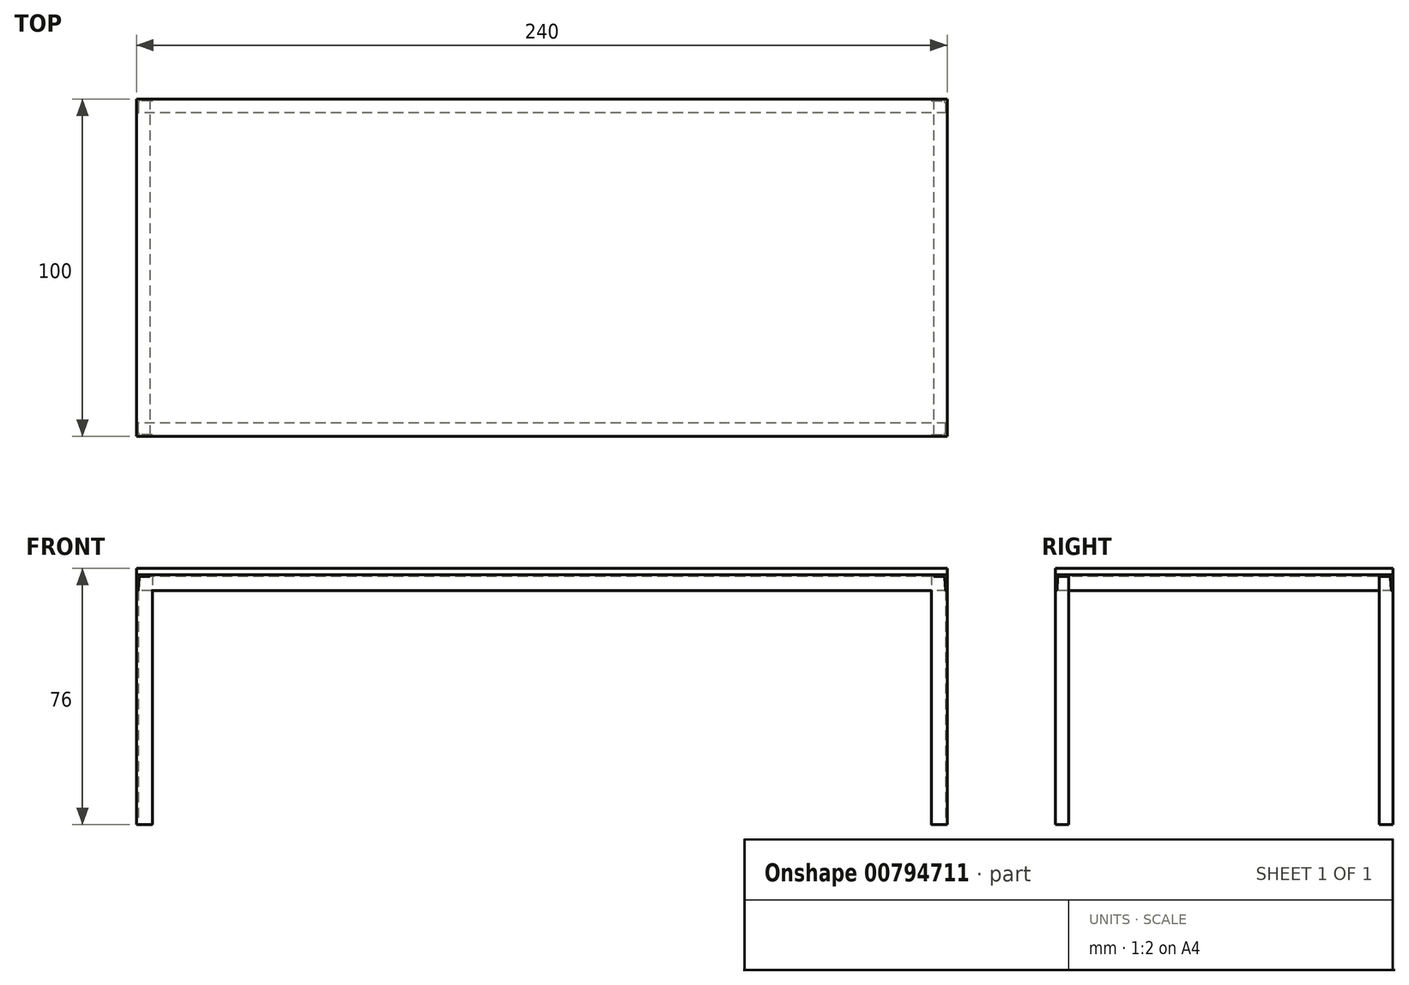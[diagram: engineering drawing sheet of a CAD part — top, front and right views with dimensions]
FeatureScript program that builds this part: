
annotation { "Feature Type Name" : "Feature", "Feature Type Description" : "" }
export const myFeature = defineFeature(function(context is Context, id is Id, definition is map)
    precondition{}
    {
        {
            var Q0;
            Q0=qCreatedBy(makeId("Top.planeOp"),FACE);
            var sketch = newSketch(context, id + "F0", { "sketchPlane" : qUnion([Q0])});
            skLineSegment(sketch, "E0", {"start": v(0, 0) * mm, "end": v(0, 4) * mm});
            skLineSegment(sketch, "E1", {"start": v(0, 4) * mm, "end": v(0, 0) * mm});
            skLineSegment(sketch, "E2", {"start": v(0, 0) * mm, "end": v(4.52, 0) * mm});
            skLineSegment(sketch, "E3", {"start": v(0.5, 1.22) * mm, "end": v(0.5, 4) * mm});
            skLineSegment(sketch, "E4", {"start": v(4.53, 0.51) * mm, "end": v(0.97, 0.72) * mm});
            skLineSegment(sketch, "E5", {"start": v(4.7, 0.33) * mm, "end": v(4.7, 0.18) * mm});
            skLineSegment(sketch, "E6", {"start": v(0, 4) * mm, "end": v(0.5, 4) * mm});
            skPoint(sketch, "E7.visualSharp", {"position": v(0.5, 0.75) * mm});
            skArc(sketch, "E7.filletArc", {"start": v(0.5, 1.22) * mm, "mid": v(0.64, 0.88) * mm, "end": v(0.97, 0.72) * mm});
            skPoint(sketch, "E8.visualSharp", {"position": v(4.7, 0.5) * mm});
            skArc(sketch, "E8.filletArc", {"start": v(4.7, 0.33) * mm, "mid": v(4.65, 0.45) * mm, "end": v(4.53, 0.51) * mm});
            skPoint(sketch, "E9.visualSharp", {"position": v(4.7, 0) * mm});
            skArc(sketch, "E9.filletArc", {"start": v(4.52, 0) * mm, "mid": v(4.65, 0.05) * mm, "end": v(4.7, 0.18) * mm});
            skSolve(sketch);
        }
        {
            var Q0;
            Q0 = qSketchRegion(id + "F0", true);
            extrude(context, id + "F1", {"entities" : qUnion([Q0]), "depth" : 74 * mm, "offsetDistance" : 25 * mm});
        }
        {
            var Q0;
            Q0=qCreatedBy(makeId("Front.planeOp"),FACE);
            cPlane(context, id + "F2", {"entities" : qUnion([Q0]), "cplaneType" : CPlaneType.OFFSET, "offset" : 50 * mm, "oppositeDirection" : true, "width" : 150 * mm, "height" : 150 * mm});
        }
        {
            var Q0;
            Q0=makeQuery(id+"F1.opExtrude","SWEPT_BODY",BODY,{"disambiguationData":[OSD([sQuery(id+"F0.wireOp",EDGE,"E1"),sQuery(id+"F0.wireOp",EDGE,"E2"),sQuery(id+"F0.wireOp",EDGE,"E3"),sQuery(id+"F0.wireOp",EDGE,"E4"),sQuery(id+"F0.wireOp",EDGE,"E5"),sQuery(id+"F0.wireOp",EDGE,"E6"),sQuery(id+"F0.wireOp",EDGE,"E7.filletArc"),sQuery(id+"F0.wireOp",EDGE,"E8.filletArc"),sQuery(id+"F0.wireOp",EDGE,"E9.filletArc")])]});
            var Q1;
            Q1=qCreatedBy(id+"F2.planeOp",FACE);
            mirror(context, id + "F3", {"entities" : qUnion([Q0]), "mirrorPlane" : qUnion([Q1])});
        }
        {
            var Q0;
            Q0=qCreatedBy(makeId("Right.planeOp"),FACE);
            cPlane(context, id + "F4", {"entities" : qUnion([Q0]), "cplaneType" : CPlaneType.OFFSET, "offset" : 120 * mm, "width" : 150 * mm, "height" : 150 * mm});
        }
        {
            var Q0;
            Q0=makeQuery(id+"F1.opExtrude","SWEPT_BODY",BODY,{"disambiguationData":[OSD([sQuery(id+"F0.wireOp",EDGE,"E1"),sQuery(id+"F0.wireOp",EDGE,"E2"),sQuery(id+"F0.wireOp",EDGE,"E3"),sQuery(id+"F0.wireOp",EDGE,"E4"),sQuery(id+"F0.wireOp",EDGE,"E5"),sQuery(id+"F0.wireOp",EDGE,"E6"),sQuery(id+"F0.wireOp",EDGE,"E7.filletArc"),sQuery(id+"F0.wireOp",EDGE,"E8.filletArc"),sQuery(id+"F0.wireOp",EDGE,"E9.filletArc")])]});
            var Q1;
            Q1=makeQuery(id+"F3.opPattern","COPY",BODY,{"derivedFrom":makeQuery(id+"F1.opExtrude","SWEPT_BODY",BODY,{"disambiguationData":[OSD([sQuery(id+"F0.wireOp",EDGE,"E1"),sQuery(id+"F0.wireOp",EDGE,"E2"),sQuery(id+"F0.wireOp",EDGE,"E3"),sQuery(id+"F0.wireOp",EDGE,"E4"),sQuery(id+"F0.wireOp",EDGE,"E5"),sQuery(id+"F0.wireOp",EDGE,"E6"),sQuery(id+"F0.wireOp",EDGE,"E7.filletArc"),sQuery(id+"F0.wireOp",EDGE,"E8.filletArc"),sQuery(id+"F0.wireOp",EDGE,"E9.filletArc")])]}),"instanceName":"1"});
            var Q2;
            Q2=qCreatedBy(id+"F4.planeOp",FACE);
            mirror(context, id + "F5", {"entities" : qUnion([Q0, Q1]), "mirrorPlane" : qUnion([Q2])});
        }
        {
            var Q0;
            Q0=qCreatedBy(makeId("Right.planeOp"),FACE);
            var sketch = newSketch(context, id + "F6", { "sketchPlane" : qUnion([Q0])});
            skArc(sketch, "E10.1.0", {"start": v(0.33, 69.3) * mm, "mid": v(0.45, 69.35) * mm, "end": v(0.51, 69.47) * mm});
            skLineSegment(sketch, "E10.1.1", {"start": v(1.22, 73.5) * mm, "end": v(4, 73.5) * mm});
            skLineSegment(sketch, "E10.1.2", {"start": v(4, 74) * mm, "end": v(0, 74) * mm});
            skLineSegment(sketch, "E10.1.3", {"start": v(4, 74) * mm, "end": v(4, 73.5) * mm});
            skLineSegment(sketch, "E10.1.4", {"start": v(0.33, 69.3) * mm, "end": v(0.18, 69.3) * mm});
            skLineSegment(sketch, "E10.1.5", {"start": v(0.51, 69.47) * mm, "end": v(0.72, 73.03) * mm});
            skArc(sketch, "E10.1.6", {"start": v(1.22, 73.5) * mm, "mid": v(0.88, 73.36) * mm, "end": v(0.72, 73.03) * mm});
            skLineSegment(sketch, "E10.1.7", {"start": v(0, 74) * mm, "end": v(0, 69.48) * mm});
            skArc(sketch, "E10.1.8", {"start": v(0, 69.48) * mm, "mid": v(0.05, 69.35) * mm, "end": v(0.18, 69.3) * mm});
            skSolve(sketch);
        }
        {
            var Q0;
            Q0=makeQuery(id+"F6.imprint","IMPRINT",FACE,{"disambiguationData":[TD([[makeQuery(id+"F6.imprint","IMPRINT",EDGE,{"derivedFrom":sQuery(id+"F6.wireOp",EDGE,"E10.1.0")}),1.0]])]});
            extrude(context, id + "F7", {"entities" : qUnion([Q0]), "depth" : 240 * mm, "offsetDistance" : 25 * mm});
        }
        {
            var Q0;
            Q0=qCreatedBy(makeId("Front.planeOp"),FACE);
            cPlane(context, id + "F8", {"entities" : qUnion([Q0]), "cplaneType" : CPlaneType.OFFSET, "offset" : 50 * mm, "oppositeDirection" : true, "width" : 150 * mm, "height" : 150 * mm});
        }
        {
            var Q0;
            Q0=makeQuery(id+"F7.opExtrude","SWEPT_BODY",BODY,{"disambiguationData":[OSD([sQuery(id+"F6.wireOp",EDGE,"E10.1.0"),sQuery(id+"F6.wireOp",EDGE,"E10.1.1"),sQuery(id+"F6.wireOp",EDGE,"E10.1.2"),sQuery(id+"F6.wireOp",EDGE,"E10.1.3"),sQuery(id+"F6.wireOp",EDGE,"E10.1.4"),sQuery(id+"F6.wireOp",EDGE,"E10.1.5"),sQuery(id+"F6.wireOp",EDGE,"E10.1.6"),sQuery(id+"F6.wireOp",EDGE,"E10.1.7"),sQuery(id+"F6.wireOp",EDGE,"E10.1.8")])]});
            var Q1;
            Q1=qCreatedBy(id+"F8.planeOp",FACE);
            mirror(context, id + "F9", {"entities" : qUnion([Q0]), "mirrorPlane" : qUnion([Q1])});
        }
        {
            var Q0;
            Q0=qCreatedBy(makeId("Front.planeOp"),FACE);
            var sketch = newSketch(context, id + "F10", { "sketchPlane" : qUnion([Q0])});
            skArc(sketch, "E11.1.0", {"start": v(0.33, 69.3) * mm, "mid": v(0.45, 69.35) * mm, "end": v(0.51, 69.47) * mm});
            skLineSegment(sketch, "E11.1.1", {"start": v(1.22, 73.5) * mm, "end": v(4, 73.5) * mm});
            skLineSegment(sketch, "E11.1.3", {"start": v(4, 74) * mm, "end": v(4, 73.5) * mm});
            skLineSegment(sketch, "E11.1.4", {"start": v(0.33, 69.3) * mm, "end": v(0.18, 69.3) * mm});
            skLineSegment(sketch, "E11.1.5", {"start": v(0.51, 69.47) * mm, "end": v(0.72, 73.03) * mm});
            skArc(sketch, "E11.1.6", {"start": v(1.22, 73.5) * mm, "mid": v(0.88, 73.36) * mm, "end": v(0.72, 73.03) * mm});
            skLineSegment(sketch, "E11.1.7", {"start": v(0, 74) * mm, "end": v(0, 69.48) * mm});
            skArc(sketch, "E11.1.8", {"start": v(0, 69.48) * mm, "mid": v(0.05, 69.35) * mm, "end": v(0.18, 69.3) * mm});
            skLineSegment(sketch, "E12", {"start": v(0, 74) * mm, "end": v(4, 74) * mm});
            skSolve(sketch);
        }
        {
            var Q0;
            Q0=makeQuery(id+"F10.imprint","IMPRINT",FACE,{"disambiguationData":[TD([[makeQuery(id+"F10.imprint","IMPRINT",EDGE,{"derivedFrom":sQuery(id+"F10.wireOp",EDGE,"E11.1.0")}),1.0]])]});
            extrude(context, id + "F11", {"entities" : qUnion([Q0]), "oppositeDirection" : true, "depth" : 100 * mm, "offsetDistance" : 25 * mm});
        }
        {
            var Q0;
            Q0=qCreatedBy(makeId("Right.planeOp"),FACE);
            cPlane(context, id + "F12", {"entities" : qUnion([Q0]), "cplaneType" : CPlaneType.OFFSET, "offset" : 120 * mm, "width" : 150 * mm, "height" : 150 * mm});
        }
        {
            var Q0;
            Q0=makeQuery(id+"F11.opExtrude","SWEPT_BODY",BODY,{"disambiguationData":[OSD([sQuery(id+"F10.wireOp",EDGE,"E11.1.0"),sQuery(id+"F10.wireOp",EDGE,"E11.1.1"),sQuery(id+"F10.wireOp",EDGE,"E11.1.3"),sQuery(id+"F10.wireOp",EDGE,"E11.1.4"),sQuery(id+"F10.wireOp",EDGE,"E11.1.5"),sQuery(id+"F10.wireOp",EDGE,"E11.1.6"),sQuery(id+"F10.wireOp",EDGE,"E11.1.7"),sQuery(id+"F10.wireOp",EDGE,"E11.1.8"),sQuery(id+"F10.wireOp",EDGE,"E12")])]});
            var Q1;
            Q1=qCreatedBy(id+"F12.planeOp",FACE);
            mirror(context, id + "F13", {"entities" : qUnion([Q0]), "mirrorPlane" : qUnion([Q1])});
        }
        {
            var Q0;
            Q0=qCreatedBy(makeId("Top.planeOp"),FACE);
            var sketch = newSketch(context, id + "F14", { "sketchPlane" : qUnion([Q0])});
            skLineSegment(sketch, "E13.bottom", {"start": v(0, 100) * mm, "end": v(240, 100) * mm});
            skLineSegment(sketch, "E13.top", {"start": v(0, 0) * mm, "end": v(240, 0) * mm});
            skLineSegment(sketch, "E13.left", {"start": v(0, 100) * mm, "end": v(0, 0) * mm});
            skLineSegment(sketch, "E13.right", {"start": v(240, 100) * mm, "end": v(240, 0) * mm});
            skSolve(sketch);
        }
        {
            var Q0;
            Q0=makeQuery(id+"F14.imprint","IMPRINT",FACE,{"disambiguationData":[TD([[makeQuery(id+"F14.imprint","IMPRINT",EDGE,{"derivedFrom":sQuery(id+"F14.wireOp",EDGE,"E13.bottom")}),-1.0]])]});
            extrude(context, id + "F15", {"entities" : qUnion([Q0]), "depth" : 76 * mm, "offsetDistance" : 25 * mm, "hasSecondDirection" : true, "secondDirectionOppositeDirection" : false, "secondDirectionDepth" : 74 * mm});
        }
    });
